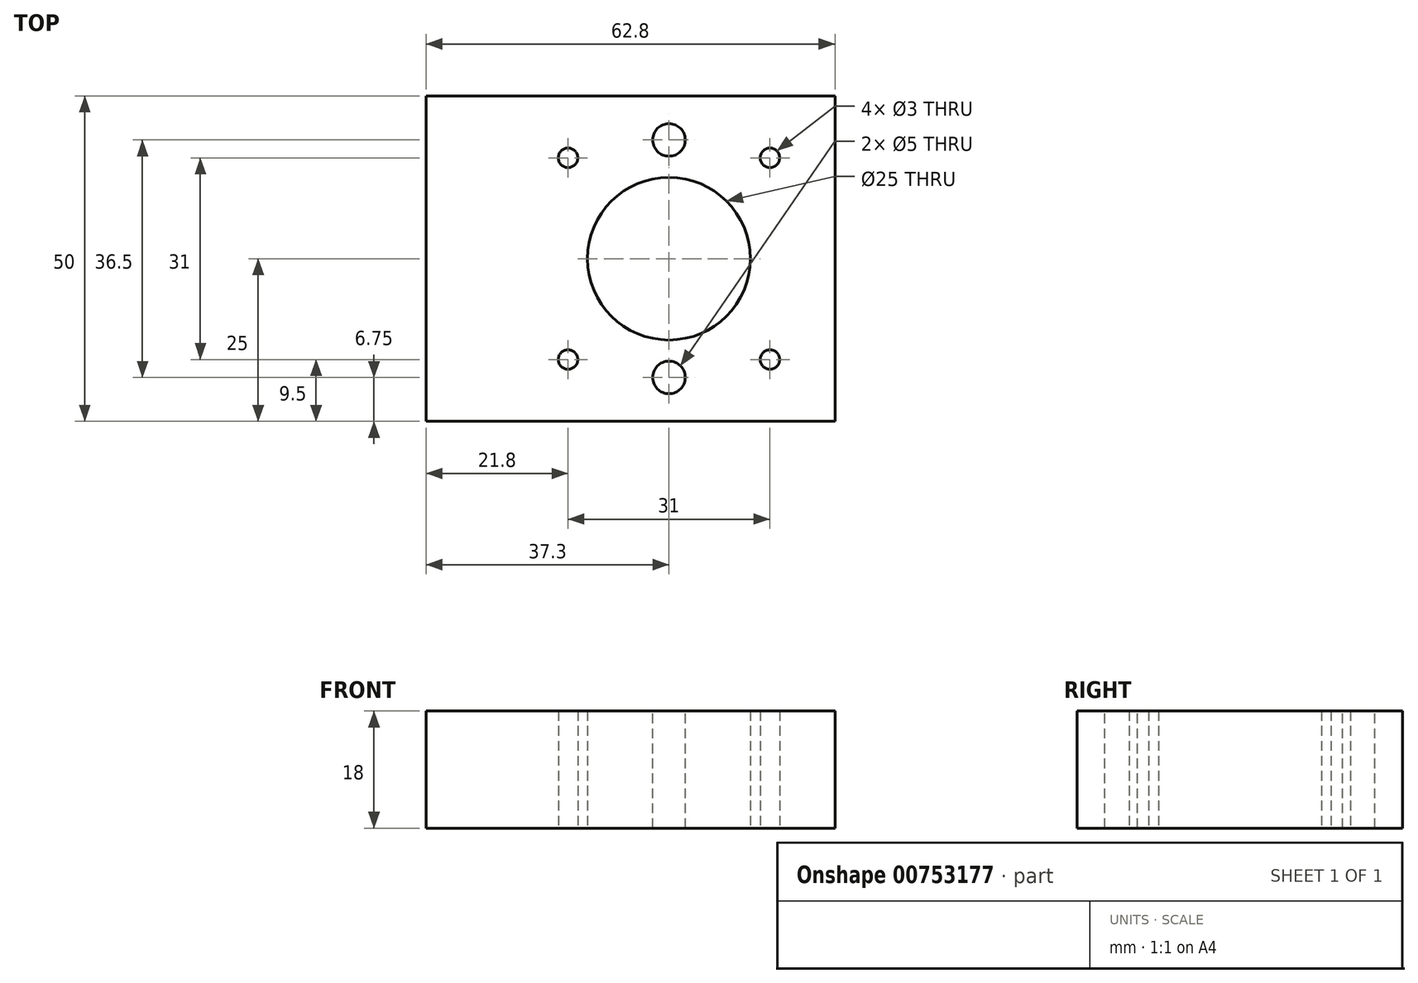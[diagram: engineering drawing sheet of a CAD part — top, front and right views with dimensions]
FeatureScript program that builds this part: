
annotation { "Feature Type Name" : "Feature", "Feature Type Description" : "" }
export const myFeature = defineFeature(function(context is Context, id is Id, definition is map)
    precondition{}
    {
        {
            var Q0;
            Q0=qCreatedBy(makeId("Top.planeOp"),FACE);
            var sketch = newSketch(context, id + "F0", { "sketchPlane" : qUnion([Q0])});
            skLineSegment(sketch, "E0.bottom", {"start": v(0, 0) * mm, "end": v(62.8, 0) * mm});
            skLineSegment(sketch, "E0.top", {"start": v(0, 50) * mm, "end": v(62.8, 50) * mm});
            skLineSegment(sketch, "E0.left", {"start": v(0, 0) * mm, "end": v(0, 50) * mm});
            skLineSegment(sketch, "E0.right", {"start": v(62.8, 0) * mm, "end": v(62.8, 50) * mm});
            skCircle(sketch, "E1", {"center": v(37.3, 25) * mm, "radius": 12.5 * mm});
            skPoint(sketch, "E1.centerSnap1", {"position": v(0, 25) * mm});
            skLineSegment(sketch, "E2", {"start": v(21.8, 40.5) * mm, "end": v(21.8, 9.5) * mm, "construction": true});
            skLineSegment(sketch, "E3", {"start": v(21.8, 9.5) * mm, "end": v(52.8, 9.5) * mm, "construction": true});
            skLineSegment(sketch, "E4", {"start": v(52.8, 9.5) * mm, "end": v(52.8, 40.5) * mm, "construction": true});
            skLineSegment(sketch, "E5", {"start": v(52.8, 40.5) * mm, "end": v(21.8, 40.5) * mm, "construction": true});
            skPoint(sketch, "E6", {"position": v(37.3, 40.5) * mm});
            skPoint(sketch, "E7", {"position": v(21.8, 25) * mm});
            skCircle(sketch, "E8", {"center": v(21.8, 40.5) * mm, "radius": 1.5 * mm});
            skCircle(sketch, "E9", {"center": v(21.8, 9.5) * mm, "radius": 1.5 * mm});
            skCircle(sketch, "E10", {"center": v(52.8, 9.5) * mm, "radius": 1.5 * mm});
            skCircle(sketch, "E11", {"center": v(52.8, 40.5) * mm, "radius": 1.5 * mm});
            skSolve(sketch);
        }
        {
            var Q0;
            Q0 = qSketchRegion(id + "F0", true);
            extrude(context, id + "F1", {"entities" : qUnion([Q0]), "depth" : 18 * mm, "offsetDistance" : 25 * mm});
        }
        {
            var Q0;
            Q0=makeQuery(id+"F1.opExtrude","CAP_FACE",FACE,{"disambiguationData":[OSD([sQuery(id+"F0.wireOp",EDGE,"E0.bottom"),sQuery(id+"F0.wireOp",EDGE,"E0.top"),sQuery(id+"F0.wireOp",EDGE,"E0.left"),sQuery(id+"F0.wireOp",EDGE,"E0.right"),sQuery(id+"F0.wireOp",EDGE,"E1"),sQuery(id+"F0.wireOp",EDGE,"E8"),sQuery(id+"F0.wireOp",EDGE,"E9"),sQuery(id+"F0.wireOp",EDGE,"E10"),sQuery(id+"F0.wireOp",EDGE,"E11")])],"isStart":false});
            var sketch = newSketch(context, id + "F2", { "sketchPlane" : qUnion([Q0])});
            skCircle(sketch, "E12", {"center": v(37.3, 43.25) * mm, "radius": 2.5 * mm});
            skLineSegment(sketch, "E13", {"start": v(37.3, 25) * mm, "end": v(37.3, 43.25) * mm, "construction": true});
            skLineSegment(sketch, "E14", {"start": v(37.3, 25) * mm, "end": v(46, 25) * mm, "construction": true});
            skCircle(sketch, "E15.MirrorC", {"center": v(37.3, 6.75) * mm, "radius": 2.5 * mm});
            skSolve(sketch);
        }
        {
            var Q0;
            Q0 = qSketchRegion(id + "F2", true);
            extrude(context, id + "F3", {"entities" : qUnion([Q0]), "operationType" : NewBodyOperationType.REMOVE, "oppositeDirection" : true, "depth" : 25 * mm, "offsetDistance" : 25 * mm});
        }
    });
